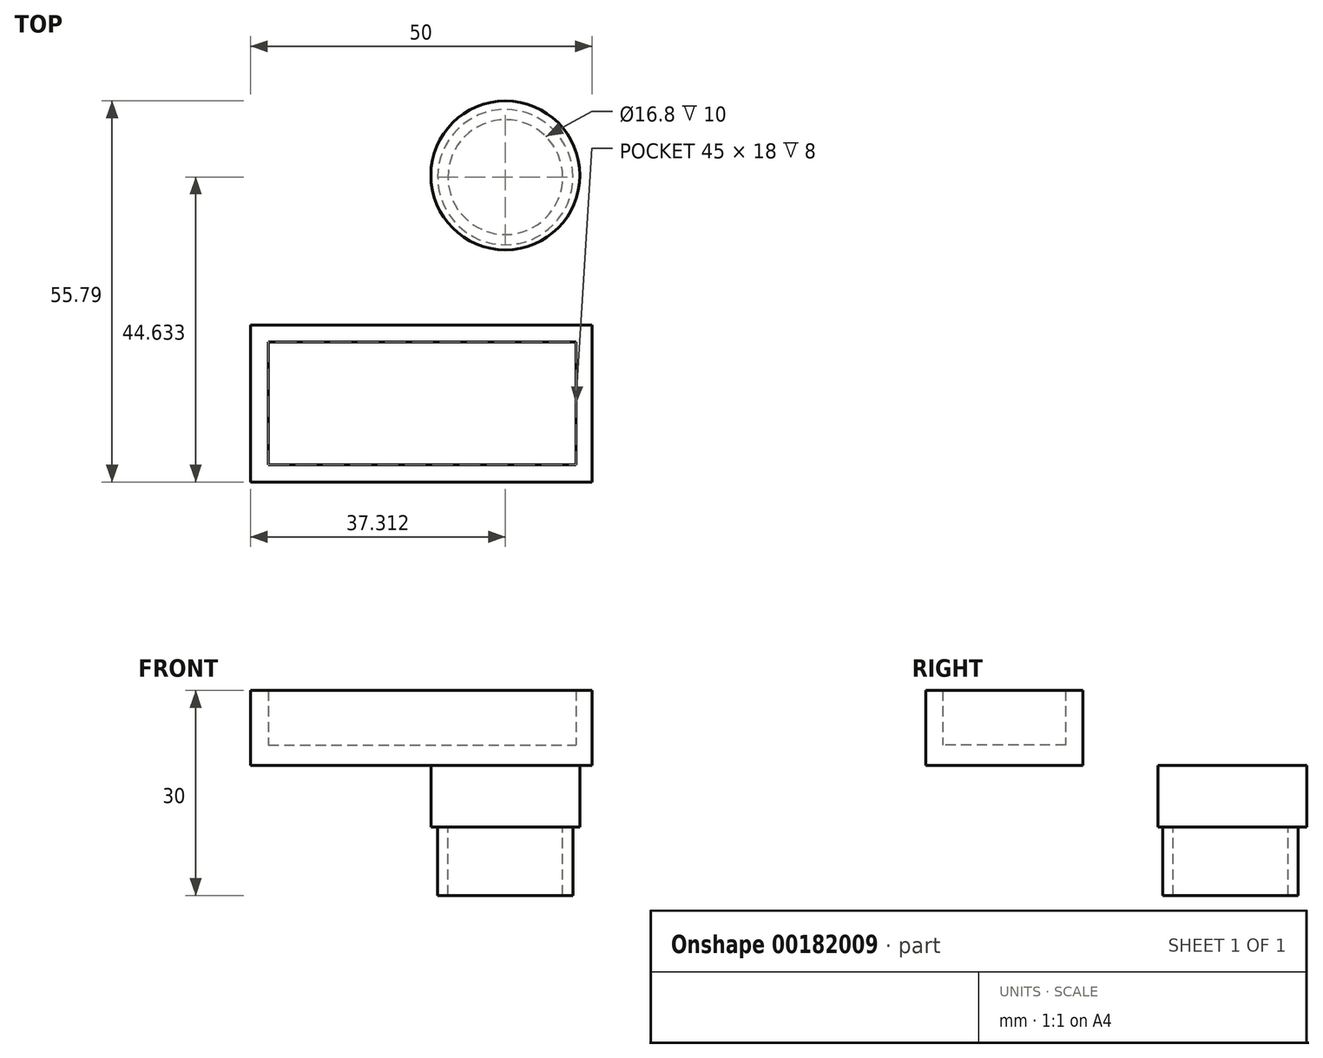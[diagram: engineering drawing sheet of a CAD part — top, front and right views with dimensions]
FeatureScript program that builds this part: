
annotation { "Feature Type Name" : "Feature", "Feature Type Description" : "" }
export const myFeature = defineFeature(function(context is Context, id is Id, definition is map)
    precondition{}
    {
        {
            var Q0;
            Q0=qCreatedBy(makeId("Top.planeOp"),FACE);
            var sketch = newSketch(context, id + "F0", { "sketchPlane" : qUnion([Q0])});
            skCircle(sketch, "E0", {"center": v(0, 0) * mm, "radius": 10.9 * mm});
            skCircle(sketch, "E1", {"center": v(0, 0) * mm, "radius": 9.9 * mm});
            skCircle(sketch, "E2", {"center": v(0, 0) * mm, "radius": 2 * mm});
            skCircle(sketch, "E3", {"center": v(0, 0) * mm, "radius": 7.5 * mm});
            skCircle(sketch, "E4", {"center": v(-26.67, 4.66) * mm, "radius": 10.9 * mm});
            skLineSegment(sketch, "E5.bottom", {"start": v(-61.32, -19.73) * mm, "end": v(-16.32, -19.73) * mm});
            skLineSegment(sketch, "E5.top", {"start": v(-61.32, -37.73) * mm, "end": v(-16.32, -37.73) * mm});
            skLineSegment(sketch, "E5.left", {"start": v(-61.32, -19.73) * mm, "end": v(-61.32, -37.73) * mm});
            skLineSegment(sketch, "E5.right", {"start": v(-16.32, -19.73) * mm, "end": v(-16.32, -37.73) * mm});
            skLineSegment(sketch, "E6.bottom", {"start": v(-63.98, -17.23) * mm, "end": v(-13.98, -17.23) * mm});
            skLineSegment(sketch, "E6.top", {"start": v(-63.98, -40.23) * mm, "end": v(-13.98, -40.23) * mm});
            skLineSegment(sketch, "E6.left", {"start": v(-63.98, -17.23) * mm, "end": v(-63.98, -40.23) * mm});
            skLineSegment(sketch, "E6.right", {"start": v(-13.98, -17.23) * mm, "end": v(-13.98, -40.23) * mm});
            skSolve(sketch);
        }
        {
            var Q0;
            Q0=qCreatedBy(makeId("Top.planeOp"),FACE);
            cPlane(context, id + "F1", {"entities" : qUnion([Q0]), "cplaneType" : CPlaneType.OFFSET, "offset" : 2 * mm, "oppositeDirection" : true, "width" : 150 * mm, "height" : 150 * mm});
        }
        {
            var Q0;
            Q0=qCreatedBy(id+"F1.planeOp",FACE);
            var sketch = newSketch(context, id + "F2", { "sketchPlane" : qUnion([Q0])});
            skCircle(sketch, "E7", {"center": v(0, 0) * mm, "radius": 2 * mm});
            skCircle(sketch, "E8", {"center": v(-26.67, 4.34) * mm, "radius": 1 * mm});
            skCircle(sketch, "E9", {"center": v(38.3, 39.41) * mm, "radius": 25 * mm});
            skSolve(sketch);
        }
        {
            var Q0;
            Q0=makeQuery(id+"F0.imprint","IMPRINT",FACE,{"disambiguationData":[TD([[makeQuery(id+"F0.imprint","IMPRINT",EDGE,{"derivedFrom":sQuery(id+"F0.wireOp",EDGE,"E4")}),1.0]])]});
            var Q1;
            Q1=makeQuery(id+"F2.imprint","IMPRINT",FACE,{"disambiguationData":[TD([[makeQuery(id+"F2.imprint","IMPRINT",EDGE,{"derivedFrom":sQuery(id+"F2.wireOp",EDGE,"E8")}),1.0]])]});
            loft(context, id + "F3", {"sheetProfilesArray" : [{ "sheetProfileEntities" : qUnion([Q0]) }, { "sheetProfileEntities" : qUnion([Q1]) }]});
        }
        {
            var Q0;
            Q0=makeQuery(id+"F0.imprint","IMPRINT",FACE,{"disambiguationData":[TD([[makeQuery(id+"F0.imprint","IMPRINT",EDGE,{"derivedFrom":sQuery(id+"F0.wireOp",EDGE,"E4")}),1.0]])]});
            extrude(context, id + "F4", {"entities" : qUnion([Q0]), "operationType" : NewBodyOperationType.ADD, "oppositeDirection" : true, "depth" : 9 * mm});
        }
        {
            var Q0;
            Q0=qCreatedBy(makeId("Top.planeOp"),FACE);
            cPlane(context, id + "F5", {"entities" : qUnion([Q0]), "cplaneType" : CPlaneType.OFFSET, "offset" : 9 * mm, "oppositeDirection" : true, "width" : 150 * mm, "height" : 150 * mm});
        }
        {
            var Q0;
            Q0=qCreatedBy(id+"F5.planeOp",FACE);
            var sketch = newSketch(context, id + "F6", { "sketchPlane" : qUnion([Q0])});
            skPoint(sketch, "E10", {"position": v(-26.67, 4.4) * mm});
            skCircle(sketch, "E11", {"center": v(-26.67, 4.4) * mm, "radius": 9.9 * mm});
            skCircle(sketch, "E12", {"center": v(-26.67, 4.4) * mm, "radius": 8.4 * mm});
            skSolve(sketch);
        }
        {
            var Q0;
            Q0=makeQuery(id+"F6.imprint","IMPRINT",FACE,{"disambiguationData":[TD([[makeQuery(id+"F6.imprint","IMPRINT",EDGE,{"derivedFrom":sQuery(id+"F6.wireOp",EDGE,"E11")}),1.0]])]});
            extrude(context, id + "F7", {"entities" : qUnion([Q0]), "operationType" : NewBodyOperationType.ADD, "oppositeDirection" : true, "depth" : 10 * mm});
        }
        {
            var Q0;
            Q0=qCreatedBy(id+"F5.planeOp",FACE);
            cPlane(context, id + "F8", {"entities" : qUnion([Q0]), "cplaneType" : CPlaneType.OFFSET, "offset" : 10 * mm, "oppositeDirection" : true, "width" : 150 * mm, "height" : 150 * mm});
        }
        {
            var Q0;
            Q0=makeQuery(id+"F0.imprint","IMPRINT",FACE,{"disambiguationData":[TD([[makeQuery(id+"F0.imprint","IMPRINT",EDGE,{"derivedFrom":sQuery(id+"F0.wireOp",EDGE,"E5.bottom")}),1.0]])]});
            extrude(context, id + "F9", {"entities" : qUnion([Q0]), "depth" : 11 * mm});
        }
        {
            var Q0;
            Q0=makeQuery(id+"F0.imprint","IMPRINT",FACE,{"disambiguationData":[TD([[makeQuery(id+"F0.imprint","IMPRINT",EDGE,{"derivedFrom":sQuery(id+"F0.wireOp",EDGE,"E5.bottom")}),-1.0]])]});
            extrude(context, id + "F10", {"entities" : qUnion([Q0]), "operationType" : NewBodyOperationType.ADD, "depth" : 3 * mm});
        }
    });
